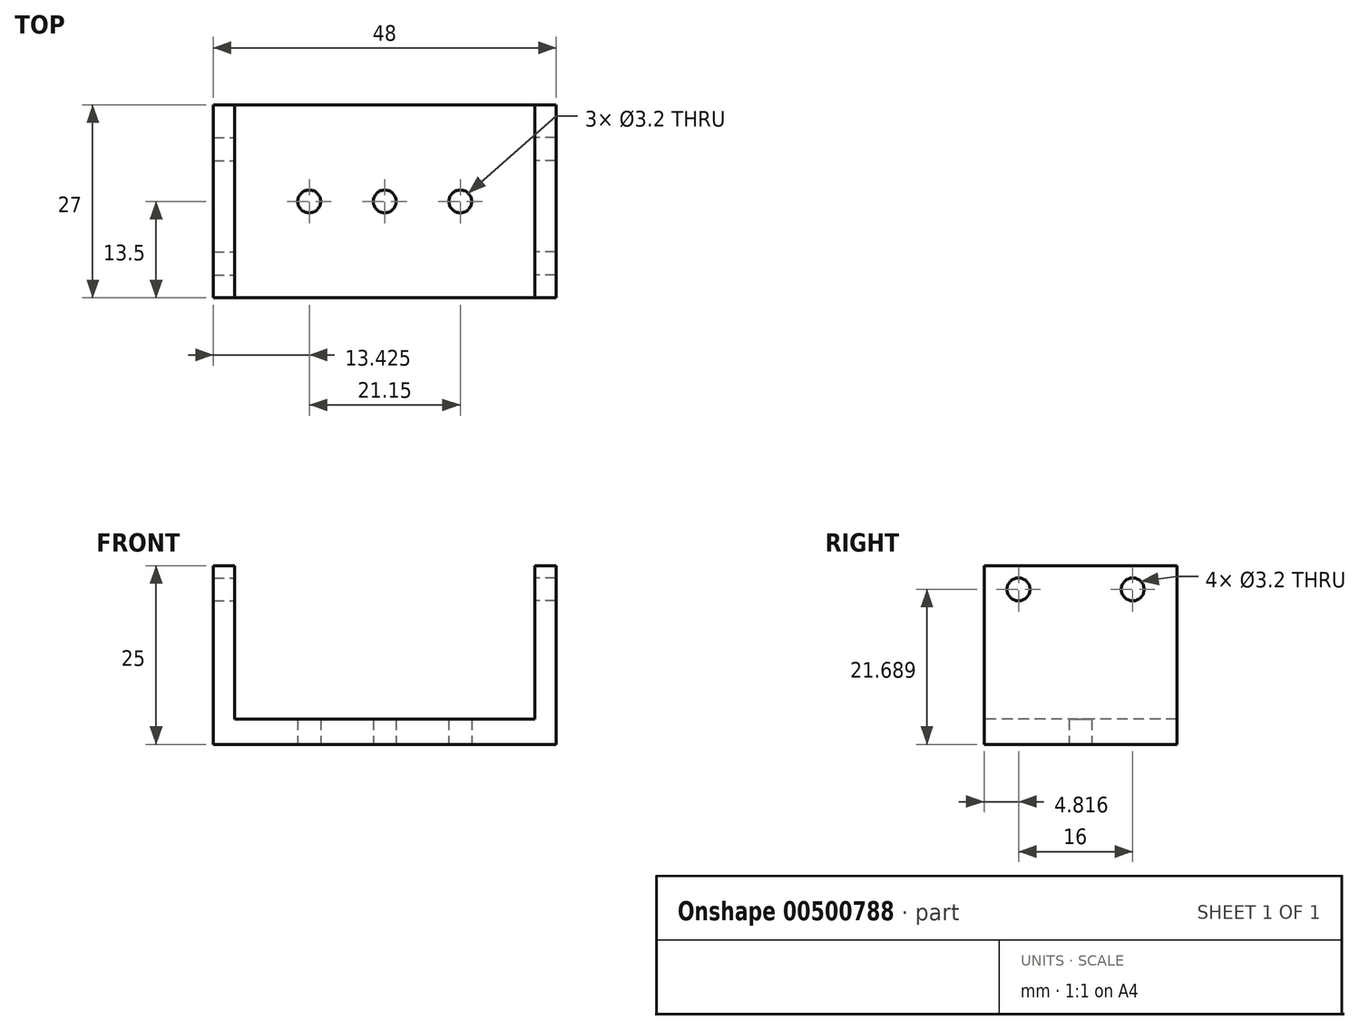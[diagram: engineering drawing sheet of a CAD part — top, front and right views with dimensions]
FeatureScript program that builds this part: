
annotation { "Feature Type Name" : "Feature", "Feature Type Description" : "" }
export const myFeature = defineFeature(function(context is Context, id is Id, definition is map)
    precondition{}
    {
        {
            var Q0;
            Q0=qCreatedBy(makeId("Top.planeOp"),FACE);
            var sketch = newSketch(context, id + "F0", { "sketchPlane" : qUnion([Q0])});
            skLineSegment(sketch, "E0.bottom", {"start": v(21, 13.5) * mm, "end": v(-21, 13.5) * mm});
            skLineSegment(sketch, "E0.top", {"start": v(21, -13.5) * mm, "end": v(-21, -13.5) * mm});
            skLineSegment(sketch, "E0.left", {"start": v(21, 13.5) * mm, "end": v(21, -13.5) * mm});
            skLineSegment(sketch, "E0.right", {"start": v(-21, 13.5) * mm, "end": v(-21, -13.5) * mm});
            skPoint(sketch, "E0.middle", {"position": v(0, 0) * mm});
            skLineSegment(sketch, "E1", {"start": v(21, -13.5) * mm, "end": v(24, -13.5) * mm});
            skLineSegment(sketch, "E2", {"start": v(24, -13.5) * mm, "end": v(24, 13.5) * mm});
            skLineSegment(sketch, "E3", {"start": v(24, 13.5) * mm, "end": v(21, 13.5) * mm});
            skLineSegment(sketch, "E4", {"start": v(-21, 13.5) * mm, "end": v(-24, 13.5) * mm});
            skLineSegment(sketch, "E5", {"start": v(-24, -13.5) * mm, "end": v(-21, -13.5) * mm});
            skLineSegment(sketch, "E6", {"start": v(-24, 13.5) * mm, "end": v(-24, -13.5) * mm});
            skLineSegment(sketch, "E7", {"start": v(0, 0) * mm, "end": v(-12.32, 0) * mm});
            skLineSegment(sketch, "E8", {"start": v(0, 0) * mm, "end": v(12.32, 0) * mm});
            skLineSegment(sketch, "E9", {"start": v(-12.32, 0) * mm, "end": v(-8.82, 0) * mm});
            skLineSegment(sketch, "E10", {"start": v(12.32, 0) * mm, "end": v(8.82, 0) * mm});
            skCircle(sketch, "E11", {"center": v(0, 0) * mm, "radius": 1.6 * mm});
            skLineSegment(sketch, "E12", {"start": v(-8.82, 0) * mm, "end": v(-10.57, 0) * mm});
            skLineSegment(sketch, "E13", {"start": v(8.82, 0) * mm, "end": v(10.57, 0) * mm});
            skCircle(sketch, "E14", {"center": v(-10.57, 0) * mm, "radius": 1.6 * mm});
            skCircle(sketch, "E15", {"center": v(10.57, 0) * mm, "radius": 1.6 * mm});
            skSolve(sketch);
        }
        {
            var Q0;
            Q0=qCreatedBy(makeId("Right.planeOp"),FACE);
            var sketch = newSketch(context, id + "F1", { "sketchPlane" : qUnion([Q0])});
            skLineSegment(sketch, "E16", {"start": v(10.82, 0) * mm, "end": v(10.82, 25) * mm});
            skLineSegment(sketch, "E17", {"start": v(-12.18, 0) * mm, "end": v(-12.18, 25) * mm});
            skLineSegment(sketch, "E18", {"start": v(-12.18, 25) * mm, "end": v(10.82, 25) * mm});
            skLineSegment(sketch, "E19", {"start": v(10.82, 25) * mm, "end": v(10.82, 21.69) * mm});
            skLineSegment(sketch, "E20", {"start": v(-12.18, 25) * mm, "end": v(-12.18, 21.69) * mm});
            skLineSegment(sketch, "E21", {"start": v(-12.18, 21.69) * mm, "end": v(-8.68, 21.69) * mm});
            skLineSegment(sketch, "E22", {"start": v(10.82, 21.69) * mm, "end": v(7.32, 21.69) * mm});
            skCircle(sketch, "E23", {"center": v(-8.68, 21.69) * mm, "radius": 1.7 * mm});
            skCircle(sketch, "E24", {"center": v(7.32, 21.69) * mm, "radius": 1.7 * mm});
            skSolve(sketch);
        }
        {
            var Q0;
            Q0=makeQuery(id+"F0.imprint","IMPRINT",FACE,{"disambiguationData":[TD([[makeQuery(id+"F0.imprint","IMPRINT",EDGE,{"derivedFrom":sQuery(id+"F0.wireOp",EDGE,"E0.bottom")}),1.0]])]});
            extrude(context, id + "F2", {"entities" : qUnion([Q0]), "depth" : 3.5 * mm, "offsetDistance" : 25 * mm});
        }
        {
            var Q0;
            Q0=makeQuery(id+"F0.imprint","IMPRINT",FACE,{"disambiguationData":[TD([[makeQuery(id+"F0.imprint","IMPRINT",EDGE,{"derivedFrom":sQuery(id+"F0.wireOp",EDGE,"E0.right")}),-1.0]])]});
            extrude(context, id + "F3", {"entities" : qUnion([Q0]), "operationType" : NewBodyOperationType.ADD, "depth" : 25 * mm, "offsetDistance" : 25 * mm});
        }
        {
            var Q0;
            Q0=makeQuery(id+"F0.imprint","IMPRINT",FACE,{"disambiguationData":[TD([[makeQuery(id+"F0.imprint","IMPRINT",EDGE,{"derivedFrom":sQuery(id+"F0.wireOp",EDGE,"E0.left")}),1.0]])]});
            extrude(context, id + "F4", {"entities" : qUnion([Q0]), "operationType" : NewBodyOperationType.ADD, "depth" : 25 * mm, "offsetDistance" : 25 * mm});
        }
        {
            var Q0;
            Q0=sQuery(id+"F1.wireOp",VERTEX,"E21.end");
            var Q1;
            Q1=makeQuery(id+"F2.opExtrude","SWEPT_BODY",BODY,{"disambiguationData":[OSD([sQuery(id+"F0.wireOp",EDGE,"E0.bottom"),sQuery(id+"F0.wireOp",EDGE,"E0.top"),sQuery(id+"F0.wireOp",EDGE,"E0.left"),sQuery(id+"F0.wireOp",EDGE,"E0.right")])]});
            hole(context, id + "F5", {"style" : HoleStyle.SIMPLE, "endStyle" : HoleEndStyle.THROUGH, "oppositeDirection" : true, "holeDiameter" : 3.2 * mm, "isTappedThrough" : true, "tappedDepth" : 12 * mm, "tapClearance" : 3, "locations" : qUnion([Q0]), "scope" : qUnion([Q1]), "majorDiameter" : 5 * mm});
        }
        {
            var Q0;
            Q0=sQuery(id+"F1.wireOp",VERTEX,"E22.end");
            var Q1;
            Q1=makeQuery(id+"F2.opExtrude","SWEPT_BODY",BODY,{"disambiguationData":[OSD([sQuery(id+"F0.wireOp",EDGE,"E0.bottom"),sQuery(id+"F0.wireOp",EDGE,"E0.top"),sQuery(id+"F0.wireOp",EDGE,"E0.left"),sQuery(id+"F0.wireOp",EDGE,"E0.right")])]});
            hole(context, id + "F6", {"style" : HoleStyle.SIMPLE, "endStyle" : HoleEndStyle.THROUGH, "oppositeDirection" : true, "holeDiameter" : 3.2 * mm, "isTappedThrough" : true, "tappedDepth" : 12 * mm, "tapClearance" : 3, "locations" : qUnion([Q0]), "scope" : qUnion([Q1]), "majorDiameter" : 5 * mm});
        }
        {
            var Q0;
            Q0=sQuery(id+"F1.wireOp",VERTEX,"E21.end");
            var Q1;
            Q1=sQuery(id+"F1.wireOp",VERTEX,"E24.center");
            var Q2;
            Q2=makeQuery(id+"F2.opExtrude","SWEPT_BODY",BODY,{"disambiguationData":[OSD([sQuery(id+"F0.wireOp",EDGE,"E0.bottom"),sQuery(id+"F0.wireOp",EDGE,"E0.top"),sQuery(id+"F0.wireOp",EDGE,"E0.left"),sQuery(id+"F0.wireOp",EDGE,"E0.right")])]});
            hole(context, id + "F7", {"style" : HoleStyle.SIMPLE, "endStyle" : HoleEndStyle.THROUGH, "holeDiameter" : 3.2 * mm, "isTappedThrough" : true, "tappedDepth" : 12 * mm, "tapClearance" : 3, "locations" : qUnion([Q0, Q1]), "scope" : qUnion([Q2]), "majorDiameter" : 5 * mm});
        }
    });
